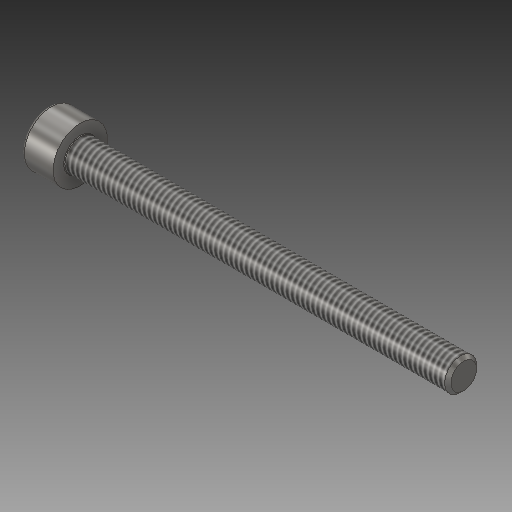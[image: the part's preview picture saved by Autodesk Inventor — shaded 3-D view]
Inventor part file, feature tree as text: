
AUTODESK INVENTOR PART (.ipt)
format: ipt  version: 2018 (Build 220112000, 112)  size: 193,536 bytes
history: native  units: mm
features: other x6, sketch x2, plane x1
ambient origin geometry x8: Origin, YZ Plane, XZ Plane, XY Plane, X Axis, Y Axis, Z Axis, Center Point
bodies: Solid1 (feature_tree)
feature tree (9):
  other  "Forged Socket Head Cap Screw - Metric M5x0.8 x 60"
  other  "Solid1::Forged Socket Head Cap Screw - Metric M5x0.8 x 60"
  other  "TaggingFeature1"
  sketch  "Sketch1"  dims[d0=10.0mm]
  sketch  "Sketch2"  dims[d19=0.0mm d28=0.0mm d29=0.0mm]
  plane  "Work Plane1"
  other  "Align 2D"
  other  "Align1"
  other  "Insert In1"
